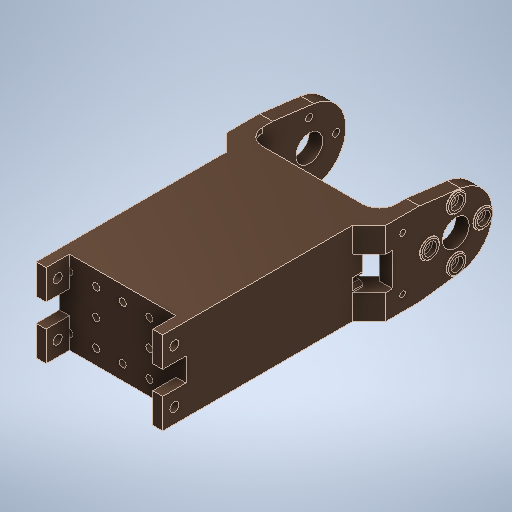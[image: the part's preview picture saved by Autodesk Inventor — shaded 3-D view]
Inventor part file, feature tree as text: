
AUTODESK INVENTOR PART (.ipt)
format: ipt  version: 2025 (Build 290162000, 162)  size: 1,291,776 bytes
history: native  units: in
note: dims shown in document units (in); Inventor stores cm internally (conversion verified against a paired STEP export)
features: extrude x4, sketch x4, other x2, direct_edit x1, imported_body x1
ambient origin geometry x8: Origin, YZ Plane, XZ Plane, XY Plane, X Axis, Y Axis, Z Axis, Center Point
bodies: Solid1 (feature_tree)
feature tree (12):
  direct_edit  "Direct Edit1"
  extrude  "Extrusion1"  Depth=0.0394in
  extrude  "Extrusión2"  Depth=0.1181in
  extrude  "Extrusión3"  Depth=0.3543in
  extrude  "Extrusión4"  Depth=0.3543in
  sketch  "Sketch1"  dims[d1=0.0394in d2=0.0394in]
  sketch  "Boceto2"  dims[d3=1.9685in d4=0.0in d7=0.1181in]
  sketch  "Boceto3"  dims[d8=0.3543in d9=0.3543in]
  sketch  "Boceto4"  dims[d10=0.1181in d11=0.3543in d12=0.1181in d13=0.2756in d14=0.0in d15=0.1063in d16=0.124in d17=0.0846in d18=0.1181in d19=0.0in d20=0.1181in d21=0.0in d22=0.6299in d23=0.0148in d24=0.5635in d25=0.0295in d26=0.8108in d27=0.0025in d28=0.0295in d29=0.0148in]
  imported_body  "Base1"
  other  "Size1"
  other  "Size2"
